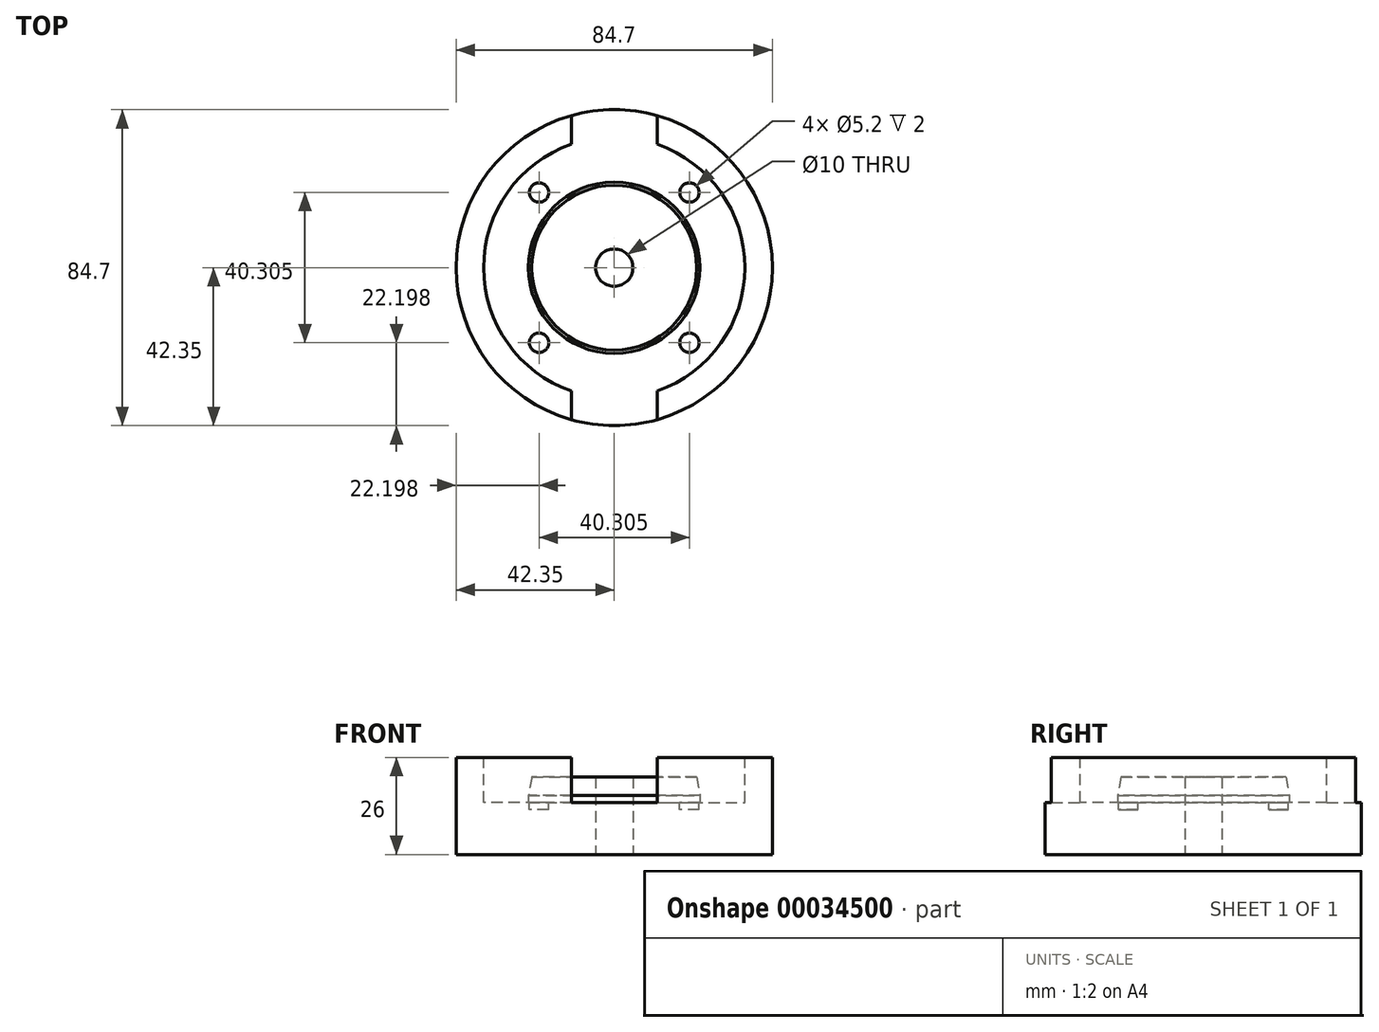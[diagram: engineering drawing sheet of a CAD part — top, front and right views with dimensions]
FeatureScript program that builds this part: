
annotation { "Feature Type Name" : "Feature", "Feature Type Description" : "" }
export const myFeature = defineFeature(function(context is Context, id is Id, definition is map)
    precondition{}
    {
        {
            var Q0;
            Q0=qCreatedBy(makeId("Top.planeOp"),FACE);
            var sketch = newSketch(context, id + "F0", { "sketchPlane" : qUnion([Q0])});
            skCircle(sketch, "E0", {"center": v(0, 0) * mm, "radius": 42.35 * mm});
            skSolve(sketch);
        }
        {
            var Q0;
            Q0 = qSketchRegion(id + "F0", true);
            extrude(context, id + "F1", {"entities" : qUnion([Q0]), "depth" : 26 * mm});
        }
        {
            var Q0;
            Q0=makeQuery(id+"F1.opExtrude","CAP_FACE",FACE,{"disambiguationData":[OSD([sQuery(id+"F0.wireOp",EDGE,"E0")])],"isStart":false});
            var sketch = newSketch(context, id + "F2", { "sketchPlane" : qUnion([Q0])});
            skCircle(sketch, "E1", {"center": v(0, 0) * mm, "radius": 35 * mm});
            skSolve(sketch);
        }
        {
            var Q0;
            Q0 = qSketchRegion(id + "F2", true);
            extrude(context, id + "F3", {"entities" : qUnion([Q0]), "operationType" : NewBodyOperationType.REMOVE, "oppositeDirection" : true, "depth" : 12 * mm});
        }
        {
            var Q0;
            Q0=qCreatedBy(makeId("Front.planeOp"),FACE);
            var sketch = newSketch(context, id + "F4", { "sketchPlane" : qUnion([Q0])});
            skLineSegment(sketch, "E2", {"start": v(0, -26.17) * mm, "end": v(0, 43.86) * mm, "construction": true});
            skSolve(sketch);
        }
        {
            var Q0;
            Q0=makeQuery(id+"F3.boolean.opBoolean","COPY",FACE,{"derivedFrom":makeQuery(id+"F3.opExtrude","CAP_FACE",FACE,{"disambiguationData":[OSD([sQuery(id+"F2.wireOp",EDGE,"E1")])],"isStart":false})});
            var sketch = newSketch(context, id + "F5", { "sketchPlane" : qUnion([Q0])});
            skLineSegment(sketch, "E3", {"start": v(0, 24.5) * mm, "end": v(0, -30.8) * mm, "construction": true});
            skSolve(sketch);
        }
        {
            var Q0;
            Q0=makeQuery(id+"F1.opExtrude","CAP_FACE",FACE,{"disambiguationData":[OSD([sQuery(id+"F0.wireOp",EDGE,"E0")])],"isStart":false});
            var sketch = newSketch(context, id + "F6", { "sketchPlane" : qUnion([Q0])});
            skLineSegment(sketch, "E4.rect.bottom", {"start": v(-11.5, -50) * mm, "end": v(11.5, -50) * mm});
            skLineSegment(sketch, "E4.rect.top", {"start": v(-11.5, 50) * mm, "end": v(11.5, 50) * mm});
            skLineSegment(sketch, "E4.rect.left", {"start": v(-11.5, -50) * mm, "end": v(-11.5, 50) * mm});
            skLineSegment(sketch, "E4.rect.right", {"start": v(11.5, -50) * mm, "end": v(11.5, 50) * mm});
            skPoint(sketch, "E4.rect.middle", {"position": v(0, 0) * mm});
            skSolve(sketch);
        }
        {
            var Q0;
            Q0 = qSketchRegion(id + "F6", true);
            extrude(context, id + "F7", {"entities" : qUnion([Q0]), "operationType" : NewBodyOperationType.REMOVE, "oppositeDirection" : true, "depth" : 12 * mm});
        }
        {
            var Q0;
            Q0=makeQuery(id+"F5.imprint","IMPRINT",FACE,{"disambiguationData":[TD([[makeQuery(id+"F5.imprint","IMPRINT",EDGE,{"derivedFrom":makeQuery(id+"F3.boolean.opBoolean","COPY",EDGE,{"derivedFrom":makeQuery(id+"F3.opExtrude","CAP_EDGE",EDGE,{"disambiguationData":[OSD([sQuery(id+"F2.wireOp",EDGE,"E1")])],"isStart":false})})}),1.0]])]});
            var sketch = newSketch(context, id + "F8", { "sketchPlane" : qUnion([Q0])});
            skCircle(sketch, "E5", {"center": v(-20.15, 20.15) * mm, "radius": 2.6 * mm});
            skCircle(sketch, "E6", {"center": v(20.15, 20.15) * mm, "radius": 2.6 * mm});
            skCircle(sketch, "E7", {"center": v(20.15, -20.15) * mm, "radius": 2.6 * mm});
            skCircle(sketch, "E8", {"center": v(-20.15, -20.15) * mm, "radius": 2.6 * mm});
            skSolve(sketch);
        }
        {
            var Q0;
            Q0 = qSketchRegion(id + "F8", true);
            extrude(context, id + "F9", {"entities" : qUnion([Q0]), "operationType" : NewBodyOperationType.REMOVE, "oppositeDirection" : true, "depth" : 2 * mm});
        }
        {
            var Q0;
            Q0=qCreatedBy(makeId("Front.planeOp"),FACE);
            var sketch = newSketch(context, id + "F10", { "sketchPlane" : qUnion([Q0])});
            skLineSegment(sketch, "E9.bottom", {"start": v(0, 20.8) * mm, "end": v(22.08, 20.8) * mm});
            skLineSegment(sketch, "E9.top", {"start": v(0, 14) * mm, "end": v(22.98, 14) * mm});
            skLineSegment(sketch, "E9.left", {"start": v(0, 20.8) * mm, "end": v(0, 14) * mm});
            skLineSegment(sketch, "E9.right", {"start": v(22.98, 15.9) * mm, "end": v(22.98, 14) * mm});
            skLineSegment(sketch, "E10", {"start": v(22.07, 20.8) * mm, "end": v(22.98, 15.9) * mm});
            skSolve(sketch);
        }
        {
            var Q0;
            Q0=makeQuery(id+"F10.imprint","IMPRINT",FACE,{"disambiguationData":[TD([[makeQuery(id+"F10.imprint","IMPRINT",EDGE,{"derivedFrom":sQuery(id+"F10.wireOp",EDGE,"E9.bottom")}),-1.0]])]});
            var Q1;
            Q1=sQuery(id+"F4.wireOp",EDGE,"E2");
            revolve(context, id + "F11", {"operationType" : NewBodyOperationType.ADD, "entities" : qUnion([Q0]), "axis" : qUnion([Q1]), "revolveType" : RevolveType.FULL});
        }
        {
            var Q0;
            Q0=makeQuery(id+"F1.opExtrude","CAP_FACE",FACE,{"disambiguationData":[OSD([sQuery(id+"F0.wireOp",EDGE,"E0")])],"isStart":true});
            var sketch = newSketch(context, id + "F12", { "sketchPlane" : qUnion([Q0])});
            skCircle(sketch, "E11", {"center": v(0, 0) * mm, "radius": 5 * mm});
            skSolve(sketch);
        }
        {
            var Q0;
            Q0 = qSketchRegion(id + "F12", true);
            extrude(context, id + "F13", {"entities" : qUnion([Q0]), "operationType" : NewBodyOperationType.REMOVE, "endBound" : BoundingType.THROUGH_ALL, "oppositeDirection" : true, "depth" : 25 * mm});
        }
    });
